# Revit family: Mop_Broom_Holder-Bradley_Corp-Stainless-995x
name_source: partatom
category: Specialty Equipment
revit_build: Autodesk Revit MEP 2012 (Build: 20110309_2315(x64)
units: mm (PartAtom-declared; Revit-internal decimal feet)

## types (3) — shared parameters
ADA Compliant = No
Accessory Material = Metal - Bradley Corp - Stainless Steel-Satin
Assembly Code = C1030300
Buy American Act = To Be Determined
DIM C = 2"
Default Elevation = 48"
Depth = 0"
Height = 0"
Installation Type = Wall Mounted
Length = 0"
Low Emitting Material = No
Manufacturer = Bradley Corporation
MasterFormat Number = 10 57 23
MasterFormat Title = Closet and Utility Shelving
OmniClass Code = 23-21 11 11 15
OmniClass Title = Commercial Storage Racking
Product Tech Data URL - English = http://bradleycorp.com
Product Tech Data URL - Spanish = http://bradleycorp.com
Specifications URL = http://www.bradleycorp.com
URL = http://www.bradleycorp.com
Version = 2.0
Width = 0"
zero-valued in all types: Percentage of Recycled Content

## per-type parameters (varying)
| type | DIM A | Description | Model |
| 9955 | 48" | Mop-Broom Holder w/5 Holders 48" W | 9955 |
| 9953-BradEX | 24" | Mop-Broom Holder w/3 Holders 24" W | 9953 BradEX |
| 9954-BradEX | 36" | Mop-Broom Holder w/4 Holders 36" W | 9954 BradEX |

## geometry (parser evidence)
native form markers: Blend x10, Sweep x4
no freeform markers — native parametric forms only
